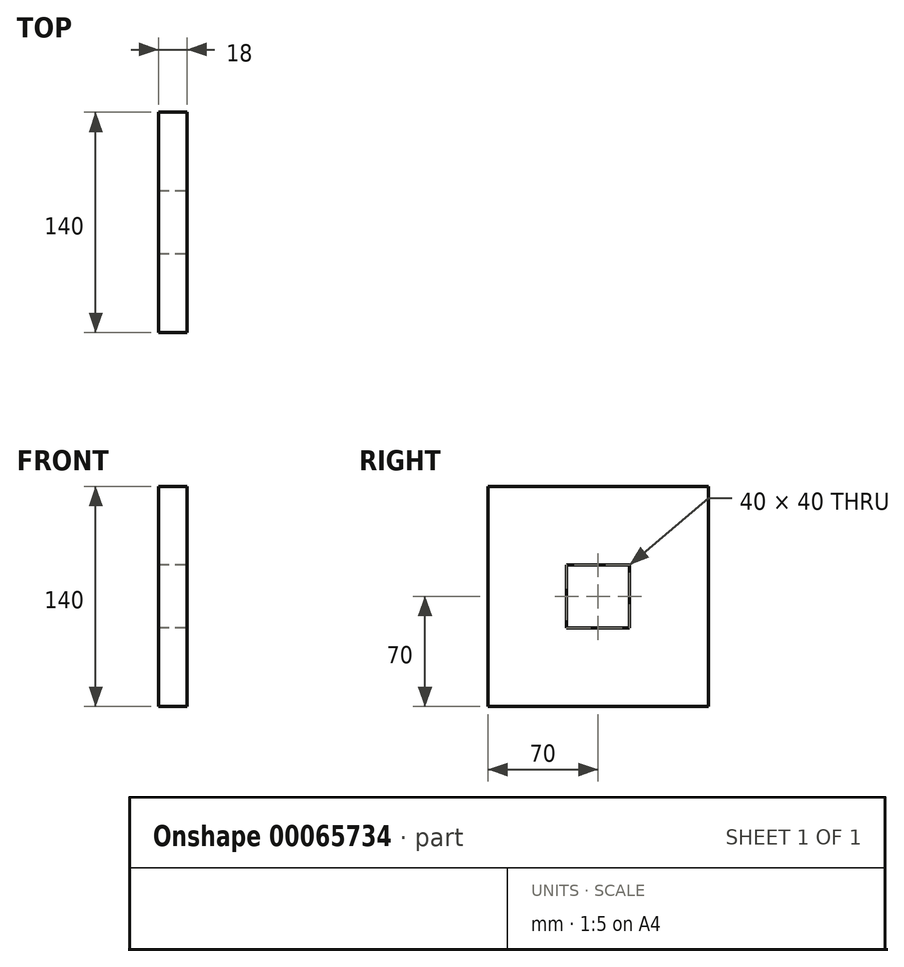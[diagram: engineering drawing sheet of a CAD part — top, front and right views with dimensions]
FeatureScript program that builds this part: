
annotation { "Feature Type Name" : "Feature", "Feature Type Description" : "" }
export const myFeature = defineFeature(function(context is Context, id is Id, definition is map)
    precondition{}
    {
        {
            var Q0;
            Q0=qCreatedBy(makeId("Right.planeOp"),FACE);
            var sketch = newSketch(context, id + "F0", { "sketchPlane" : qUnion([Q0])});
            skLineSegment(sketch, "E0.bottom", {"start": v(0, 0) * mm, "end": v(-140, 0) * mm});
            skLineSegment(sketch, "E0.top", {"start": v(0, -140) * mm, "end": v(-140, -140) * mm});
            skLineSegment(sketch, "E0.left", {"start": v(0, 0) * mm, "end": v(0, -140) * mm});
            skLineSegment(sketch, "E0.right", {"start": v(-140, 0) * mm, "end": v(-140, -140) * mm});
            skLineSegment(sketch, "E1.bottom", {"start": v(-50, -50) * mm, "end": v(-90, -50) * mm});
            skLineSegment(sketch, "E1.top", {"start": v(-50, -90) * mm, "end": v(-90, -90) * mm});
            skLineSegment(sketch, "E1.left", {"start": v(-50, -50) * mm, "end": v(-50, -90) * mm});
            skLineSegment(sketch, "E1.right", {"start": v(-90, -50) * mm, "end": v(-90, -90) * mm});
            skSolve(sketch);
        }
        {
            var Q0;
            Q0=qSketchRegion(id+"F0",true);
            extrude(context, id + "F1", {"entities" : qUnion([Q0]), "depth" : 18 * mm});
        }
    });
